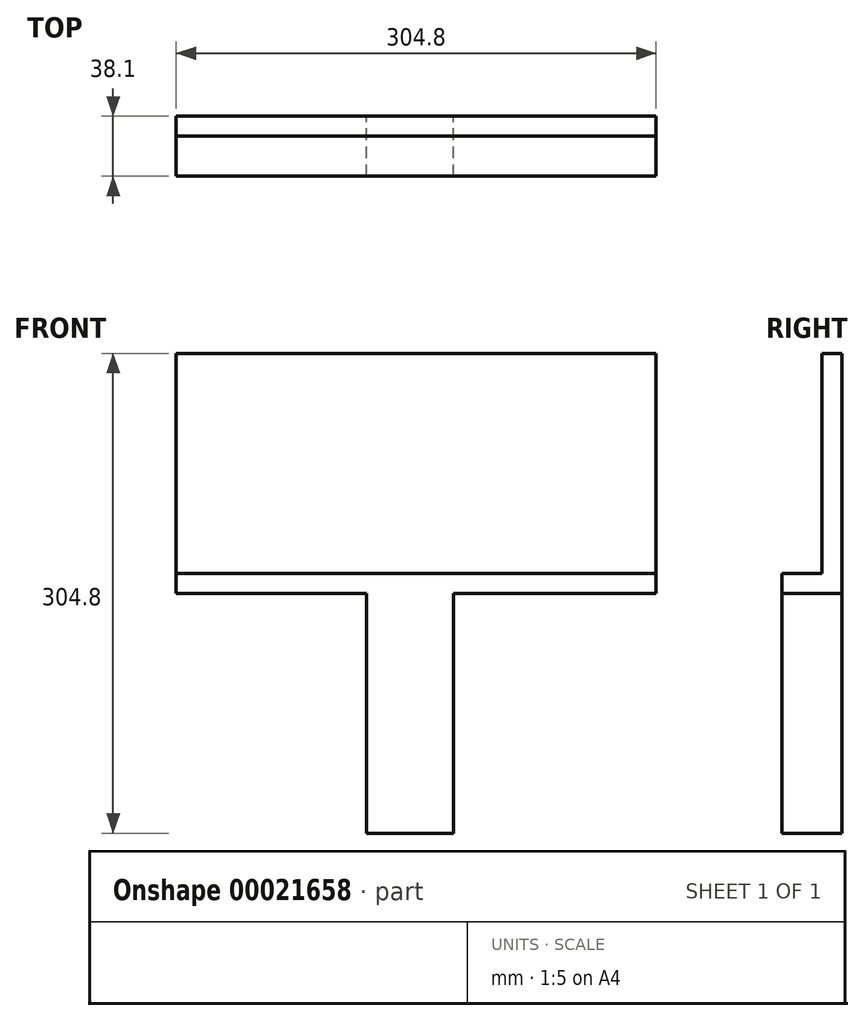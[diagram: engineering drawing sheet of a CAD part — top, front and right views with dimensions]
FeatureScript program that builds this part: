
annotation { "Feature Type Name" : "Feature", "Feature Type Description" : "" }
export const myFeature = defineFeature(function(context is Context, id is Id, definition is map)
    precondition{}
    {
        {
            var Q0;
            Q0=qCreatedBy(makeId("Front.planeOp"),FACE);
            var sketch = newSketch(context, id + "F0", { "sketchPlane" : qUnion([Q0])});
            skLineSegment(sketch, "E0.bottom", {"start": v(-154.08, 106.63) * mm, "end": v(150.72, 106.63) * mm});
            skLineSegment(sketch, "E0.top", {"start": v(-154.08, -45.77) * mm, "end": v(150.72, -45.77) * mm});
            skLineSegment(sketch, "E0.left", {"start": v(-154.08, 106.63) * mm, "end": v(-154.08, -45.77) * mm});
            skLineSegment(sketch, "E0.right", {"start": v(150.72, 106.63) * mm, "end": v(150.72, -45.77) * mm});
            skSolve(sketch);
        }
        {
            var Q0;
            Q0=makeQuery(id+"F0.imprint","IMPRINT",FACE,{"disambiguationData":[TD([[makeQuery(id+"F0.imprint","IMPRINT",EDGE,{"derivedFrom":sQuery(id+"F0.wireOp",EDGE,"E0.bottom")}),-1.0]])]});
            extrude(context, id + "F1", {"entities" : qUnion([Q0]), "depth" : 12.7 * mm});
        }
        {
            var Q0;
            Q0=makeQuery(id+"F1.opExtrude","CAP_FACE",FACE,{"disambiguationData":[OSD([sQuery(id+"F0.wireOp",EDGE,"E0.bottom"),sQuery(id+"F0.wireOp",EDGE,"E0.top"),sQuery(id+"F0.wireOp",EDGE,"E0.left"),sQuery(id+"F0.wireOp",EDGE,"E0.right")])],"isStart":false});
            var sketch = newSketch(context, id + "F2", { "sketchPlane" : qUnion([Q0])});
            skLineSegment(sketch, "E1.bottom", {"start": v(-154.08, -45.77) * mm, "end": v(150.72, -45.77) * mm});
            skLineSegment(sketch, "E1.top", {"start": v(-154.08, -33.07) * mm, "end": v(150.72, -33.07) * mm});
            skLineSegment(sketch, "E1.left", {"start": v(-154.08, -45.77) * mm, "end": v(-154.08, -33.07) * mm});
            skLineSegment(sketch, "E1.right", {"start": v(150.72, -45.77) * mm, "end": v(150.72, -33.07) * mm});
            skSolve(sketch);
        }
        {
            var Q0;
            Q0=makeQuery(id+"F2.imprint","IMPRINT",FACE,{"disambiguationData":[TD([[makeQuery(id+"F2.imprint","IMPRINT",EDGE,{"derivedFrom":sQuery(id+"F2.wireOp",EDGE,"E1.bottom")}),1.0]])]});
            extrude(context, id + "F3", {"entities" : qUnion([Q0]), "operationType" : NewBodyOperationType.ADD, "depth" : 25.4 * mm});
        }
        {
            var Q0;
            Q0=makeQuery(id+"F3.boolean.opBoolean","MERGE",FACE,{"derivedFrom":[makeQuery(id+"F1.opExtrude","SWEPT_FACE",FACE,{"disambiguationData":[OSD([sQuery(id+"F0.wireOp",EDGE,"E0.top")])]}),makeQuery(id+"F3.opExtrude","SWEPT_FACE",FACE,{"disambiguationData":[OSD([sQuery(id+"F2.wireOp",EDGE,"E1.bottom")])]})]});
            var sketch = newSketch(context, id + "F4", { "sketchPlane" : qUnion([Q0])});
            skLineSegment(sketch, "E2.bottom", {"start": v(-33.04, 38.1) * mm, "end": v(21.97, 38.1) * mm});
            skLineSegment(sketch, "E2.top", {"start": v(-33.04, 0) * mm, "end": v(21.97, 0) * mm});
            skLineSegment(sketch, "E2.left", {"start": v(-33.04, 38.1) * mm, "end": v(-33.04, 0) * mm});
            skLineSegment(sketch, "E2.right", {"start": v(21.97, 38.1) * mm, "end": v(21.97, 0) * mm});
            skSolve(sketch);
        }
        {
            var Q0;
            Q0=makeQuery(id+"F4.imprint","IMPRINT",FACE,{"disambiguationData":[TD([[makeQuery(id+"F4.imprint","IMPRINT",EDGE,{"derivedFrom":sQuery(id+"F4.wireOp",EDGE,"E2.bottom")}),-1.0]])]});
            extrude(context, id + "F5", {"entities" : qUnion([Q0]), "operationType" : NewBodyOperationType.ADD, "depth" : 152.4 * mm});
        }
    });
